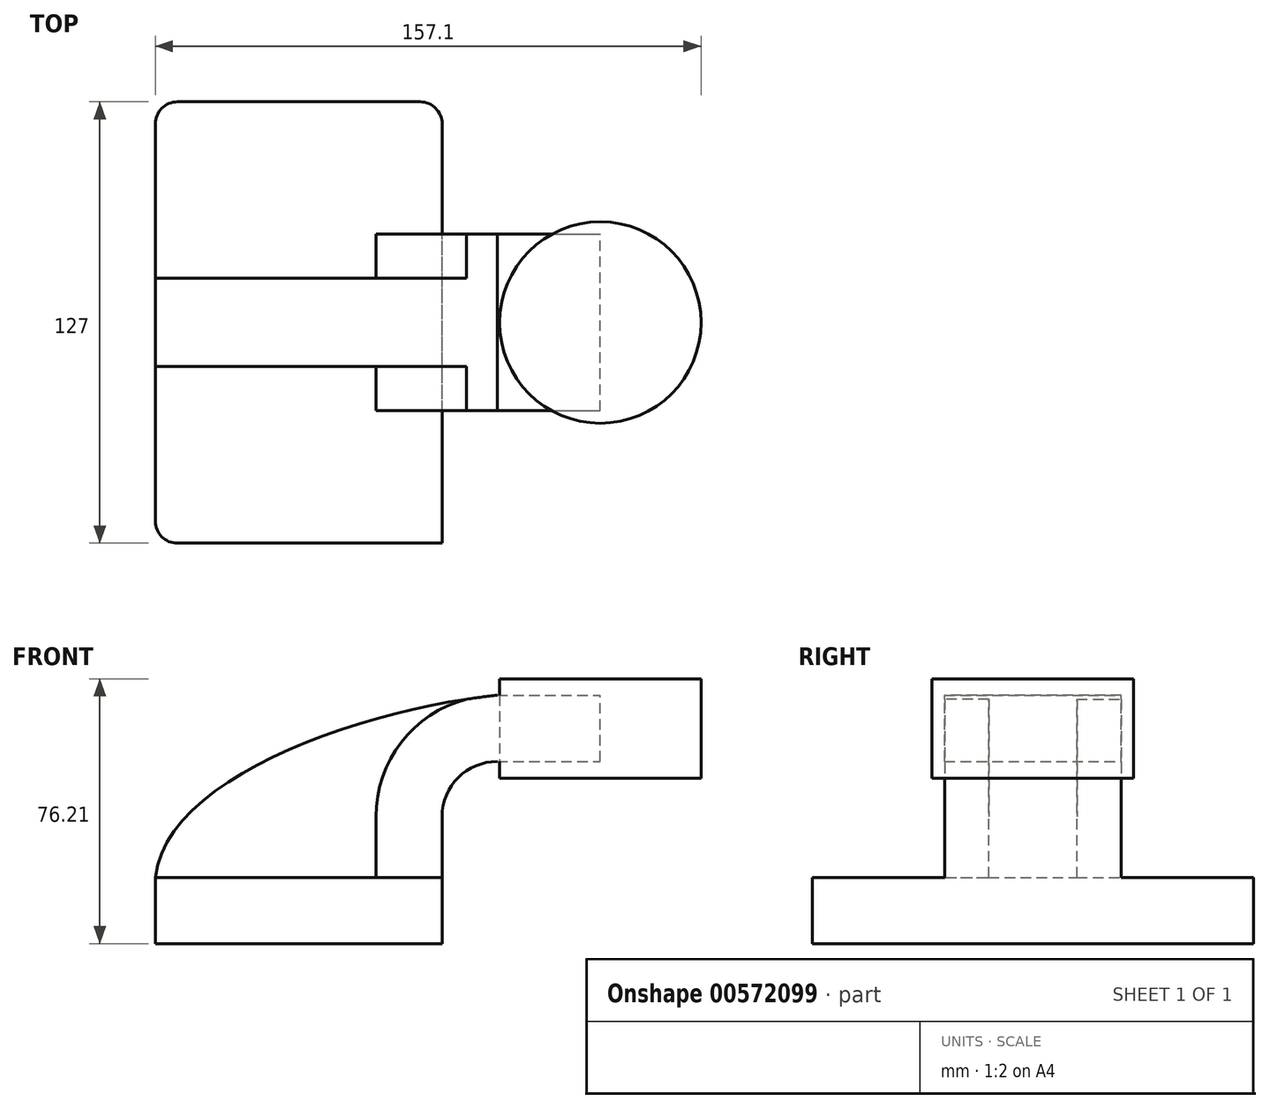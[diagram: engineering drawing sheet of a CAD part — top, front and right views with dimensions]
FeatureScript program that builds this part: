
annotation { "Feature Type Name" : "Feature", "Feature Type Description" : "" }
export const myFeature = defineFeature(function(context is Context, id is Id, definition is map)
    precondition{}
    {
        {
            var Q0;
            Q0=qCreatedBy(makeId("Front.planeOp"),FACE);
            var sketch = newSketch(context, id + "F0", { "sketchPlane" : qUnion([Q0])});
            skLineSegment(sketch, "E0.bottom", {"start": v(-41.28, 9.52) * mm, "end": v(41.27, 9.53) * mm});
            skLineSegment(sketch, "E0.top", {"start": v(-41.28, -9.52) * mm, "end": v(41.28, -9.52) * mm});
            skLineSegment(sketch, "E0.left", {"start": v(-41.28, 9.52) * mm, "end": v(-41.28, -9.53) * mm});
            skLineSegment(sketch, "E0.right", {"start": v(41.27, 9.53) * mm, "end": v(41.28, -9.52) * mm});
            skPoint(sketch, "E0.middle", {"position": v(0, 0) * mm});
            skLineSegment(sketch, "E1.bottom", {"start": v(65.02, 38.1) * mm, "end": v(115.82, 38.1) * mm});
            skLineSegment(sketch, "E1.top", {"start": v(65.02, 66.68) * mm, "end": v(115.82, 66.68) * mm});
            skLineSegment(sketch, "E1.left", {"start": v(65.02, 38.1) * mm, "end": v(65.02, 66.68) * mm});
            skLineSegment(sketch, "E1.right", {"start": v(115.82, 38.1) * mm, "end": v(115.82, 66.68) * mm});
            skPoint(sketch, "E1.middle", {"position": v(90.42, 52.39) * mm});
            skLineSegment(sketch, "E2", {"start": v(41.27, 9.53) * mm, "end": v(41.27, 27) * mm});
            skArc(sketch, "E3", {"start": v(57.15, 42.88) * mm, "mid": v(45.92, 38.23) * mm, "end": v(41.27, 27) * mm});
            skLineSegment(sketch, "E4", {"start": v(57.15, 42.88) * mm, "end": v(86.83, 42.88) * mm});
            skLineSegment(sketch, "E5.0", {"start": v(57.15, 61.93) * mm, "end": v(86.83, 61.93) * mm});
            skArc(sketch, "E5.1", {"start": v(57.15, 61.93) * mm, "mid": v(32.45, 51.7) * mm, "end": v(22.23, 27) * mm});
            skLineSegment(sketch, "E5.2", {"start": v(22.23, 9.53) * mm, "end": v(22.23, 27) * mm});
            skFitSpline(sketch, "E6", {"points": [v(-41.28, 9.53) * mm, v(57.15, 61.93) * mm], "startDerivative": vector(9.44, 86.76) * mm, "endDerivative": vector(117.58, 12.21) * mm});
            skLineSegment(sketch, "E7", {"start": v(86.83, 38.1) * mm, "end": v(86.83, 66.68) * mm});
            skSolve(sketch);
        }
        {
            var Q0;
            Q0=makeQuery(id+"F0.imprint","IMPRINT",FACE,{"disambiguationData":[TD([[makeQuery(id+"F0.imprint","IMPRINT",EDGE,{"derivedFrom":sQuery(id+"F0.wireOp",EDGE,"E0.top")}),1.0]])]});
            extrude(context, id + "F1", {"entities" : qUnion([Q0]), "endBound" : BoundingType.SYMMETRIC, "depth" : 127 * mm, "offsetDistance" : 25.4 * mm});
        }
        {
            var Q0;
            {var subQ1=sQuery(id+"F0.wireOp",EDGE,"E2");Q0=makeQuery(id+"F0.imprint","IMPRINT",FACE,{"disambiguationData":[TD([[makeQuery(id+"F0.imprint","IMPRINT",EDGE,{"derivedFrom":subQ1}),1.0]])]});}
            var Q1;
            {var subQ0=sQuery(id+"F0.wireOp",EDGE,"E4");var subQ1=sQuery(id+"F0.wireOp",EDGE,"E1.left");var subQ2=makeQuery(id+"F0.imprint","INTERSECT",VERTEX,{"derivedFrom":[subQ1,subQ0]});Q1=makeQuery(id+"F0.imprint","IMPRINT",FACE,{"disambiguationData":[TD([[makeQuery(id+"F0.imprint","IMPRINT",EDGE,{"disambiguationData":[TD([[subQ2,-1.0]])],"derivedFrom":subQ1}),-1.0]])]});}
            extrude(context, id + "F2", {"entities" : qUnion([Q0, Q1]), "operationType" : NewBodyOperationType.ADD, "endBound" : BoundingType.SYMMETRIC, "depth" : 50.8 * mm, "offsetDistance" : 25.4 * mm});
        }
        {
            var Q0;
            {var subQ3=sQuery(id+"F0.wireOp",EDGE,"E5.2");Q0=makeQuery(id+"F0.imprint","IMPRINT",FACE,{"disambiguationData":[TD([[makeQuery(id+"F0.imprint","IMPRINT",EDGE,{"derivedFrom":subQ3}),1.0]])]});}
            extrude(context, id + "F3", {"entities" : qUnion([Q0]), "operationType" : NewBodyOperationType.ADD, "endBound" : BoundingType.SYMMETRIC, "depth" : 25.4 * mm, "offsetDistance" : 25.4 * mm});
        }
        {
            var Q0;
            {var subQ4=sQuery(id+"F0.wireOp",EDGE,"E1.right");Q0=makeQuery(id+"F0.imprint","IMPRINT",FACE,{"disambiguationData":[TD([[makeQuery(id+"F0.imprint","IMPRINT",EDGE,{"derivedFrom":subQ4}),1.0]])]});}
            var Q1;
            Q1=sQuery(id+"F0.wireOp",EDGE,"E7");
            revolve(context, id + "F4", {"entities" : qUnion([Q0]), "axis" : qUnion([Q1]), "revolveType" : RevolveType.FULL});
        }
        {
            var Q0;
            Q0=makeQuery(id+"F1.opExtrude","CAP_EDGE",EDGE,{"disambiguationData":[OSD([sQuery(id+"F0.wireOp",EDGE,"E0.right")])],"isStart":true});
            var Q1;
            Q1=makeQuery(id+"F1.opExtrude","CAP_EDGE",EDGE,{"disambiguationData":[OSD([sQuery(id+"F0.wireOp",EDGE,"E0.left")])],"isStart":true});
            var Q2;
            Q2=makeQuery(id+"F1.opExtrude","CAP_EDGE",EDGE,{"disambiguationData":[OSD([sQuery(id+"F0.wireOp",EDGE,"E0.left")])],"isStart":false});
            fillet(context, id + "F5", {"entities" : qUnion([Q0, Q1, Q2]), "radius" : 6.35 * mm, "tangentPropagation" : true, "allowEdgeOverflow" : false});
        }
    });
